# Revit family: P201003KC-009c_KEWS105BPA
name_source: partatom
category: Specialty Equipment
units: mm (PartAtom-declared; Revit-internal decimal feet)

## family parameters
Always vertical = Yes
Cut with Voids When Loaded = No
Maintain Annotation Orientation = No
Part Type = Normal
Room Calculation Point = No
Round Connector Dimension = Use Diameter
Shared = No
Work Plane-Based = No

## types (1)
- KEWS105BPA
    Amps = 15 A
    Apparent Load = 0 VA
    Body Material = ARCAT - Metal - Steel - Stainless
    Default Elevation = 0"
    Depth = 26"
    Dimension Guide = https://www.kitchenaid.com
    Door Material = ARCAT - Wood Cream
    Family Name = warming drawer
    Feature 1 = Panel-Ready Design
    Feature 2 = Slow Cook Function
    Feature 3 = Custom-Control Technology
    Handle Material = ARCAT - Metal - Steel - Stainless
    Height = 10 1/4"
    Installation-Fabrication = https://www.kitchenaid.com
    Manufacturer = KitchenAid
    Model = KEWS105BPA
    Voltage = 0 V
    Width = 29 3/4"

## geometry (parser evidence)
native form markers: Sweep x2
no freeform markers — native parametric forms only
